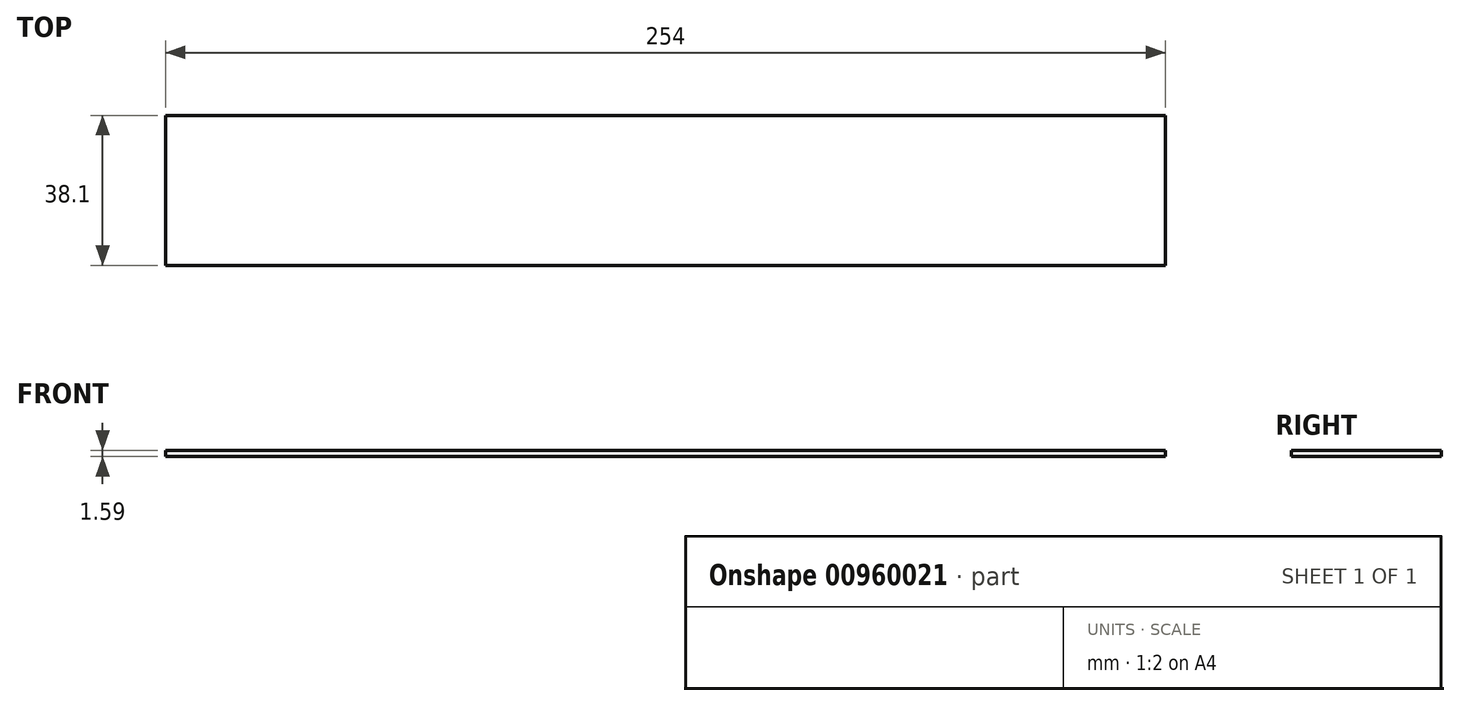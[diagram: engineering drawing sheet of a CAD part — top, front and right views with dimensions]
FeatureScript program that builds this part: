
annotation { "Feature Type Name" : "Feature", "Feature Type Description" : "" }
export const myFeature = defineFeature(function(context is Context, id is Id, definition is map)
    precondition{}
    {
        {
            var Q0;
            Q0=qCreatedBy(makeId("Top.planeOp"),FACE);
            var sketch = newSketch(context, id + "F0", { "sketchPlane" : qUnion([Q0])});
            skLineSegment(sketch, "E0.bottom", {"start": v(127, -19.05) * mm, "end": v(-127, -19.05) * mm});
            skLineSegment(sketch, "E0.top", {"start": v(127, 19.05) * mm, "end": v(-127, 19.05) * mm});
            skLineSegment(sketch, "E0.left", {"start": v(127, -19.05) * mm, "end": v(127, 19.05) * mm});
            skLineSegment(sketch, "E0.right", {"start": v(-127, -19.05) * mm, "end": v(-127, 19.05) * mm});
            skPoint(sketch, "E0.middle", {"position": v(0, 0) * mm});
            skSolve(sketch);
        }
        {
            var Q0;
            Q0=makeQuery(id+"F0.imprint","IMPRINT",FACE,{"disambiguationData":[TD([[makeQuery(id+"F0.imprint","IMPRINT",EDGE,{"derivedFrom":sQuery(id+"F0.wireOp",EDGE,"E0.bottom")}),-1.0]])]});
            extrude(context, id + "F1", {"entities" : qUnion([Q0]), "depth" : 1.59 * mm, "offsetDistance" : 25.4 * mm});
        }
    });
